# Revit family: Haworth_Compose_Panel_Glass
name_source: partatom
category: Furniture Systems
revit_build: Autodesk Revit 2018 (Build: 20170223_1515(x64)
units: mm (PartAtom-declared; Revit-internal decimal feet)

## family parameters
Always vertical = Yes
Cut with Voids When Loaded = No
OmniClass Number = 23.40.70.14.64.21
OmniClass Title = Systems Furniture
Part Type = Normal
Room Calculation Point = No
Round Connector Dimension = Use Diameter
Shared = No
Work Plane-Based = No

## types (60) — shared parameters
Assembly Code = E2020500
Bottom Trim Width = 1 1/2"
Custom Size = No
Description = Haworth Compose Panel Glass
Frame Depth = 2 3/4"
Frame Width = 3/4"
Glass Finish = Haworth _ Glass _ Clear
Manufacturer = Haworth
Max. Height = 74"
Max. Width = 48"
Min. Height = 42"
Min. Width = 18"
Min/Max Height = 42-74 in. @ 8 in. Increments
Min/Max Width = 18-48 in. @ 6 in. Increments
Model = VZGF
Panel Depth = 1/2"
Raceway Finish = Haworth _ Paint _ Putty
Revision Number = 4
Size = Verify Final Dim. w/ Haworth
Sustainability Info = http://media.haworth.com
Top Trim = Yes
Top Trim Adjuster = 1/8"
Top Trim Width = 1/8"
Trim Depth = 3"
Trim Finish = Haworth _ Paint _ Putty
Trim Thin Profile = Yes
URL = http://www.haworth.com
URL - Product = http://www.haworth.com
Vertical Trim Width = 1/4"
Warranty = http://www.haworth.com

## per-type parameters (varying)
| type | Actual Height | Actual Width | Height | Panel Height | Panel Width | Raceway | Raceway Height | Width |
| 42h 18w No Base Raceway | 41 7/8" | 18" | 42" | 33 3/4" | 16 1/2" | No | 6" | 18" |
| 42h 24w No Base Raceway | 41 7/8" | 24" | 42" | 33 3/4" | 22 1/2" | No | 6" | 24" |
| 42h 30w No Base Raceway | 41 7/8" | 30" | 42" | 33 3/4" | 28 1/2" | No | 6" | 30" |
| 42h 36w No Base Raceway | 41 7/8" | 36" | 42" | 33 3/4" | 34 1/2" | No | 6" | 36" |
| 42h 42w No Base Raceway | 41 7/8" | 42" | 42" | 33 3/4" | 40 1/2" | No | 6" | 42" |
| 42h 48w No Base Raceway | 41 7/8" | 48" | 42" | 33 3/4" | 46 1/2" | No | 6" | 48" |
| 50h 18w No Base Raceway | 49 7/8" | 18" | 50" | 41 3/4" | 16 1/2" | No | 6" | 18" |
| 50h 24w No Base Raceway | 49 7/8" | 24" | 50" | 41 3/4" | 22 1/2" | No | 6" | 24" |
| 50h 30w No Base Raceway | 49 7/8" | 30" | 50" | 41 3/4" | 28 1/2" | No | 6" | 30" |
| 50h 36w No Base Raceway | 49 7/8" | 36" | 50" | 41 3/4" | 34 1/2" | No | 6" | 36" |
| 50h 42w No Base Raceway | 49 7/8" | 42" | 50" | 41 3/4" | 40 1/2" | No | 6" | 42" |
| 50h 48w No Base Raceway | 49 7/8" | 48" | 50" | 41 3/4" | 46 1/2" | No | 6" | 48" |
| 58h 18w No Base Raceway | 57 7/8" | 18" | 58" | 49 3/4" | 16 1/2" | No | 6" | 18" |
| 58h 24w No Base Raceway | 57 7/8" | 24" | 58" | 49 3/4" | 22 1/2" | No | 6" | 24" |
| 58h 30w No Base Raceway | 57 7/8" | 30" | 58" | 49 3/4" | 28 1/2" | No | 6" | 30" |
| 58h 36w No Base Raceway | 57 7/8" | 36" | 58" | 49 3/4" | 34 1/2" | No | 6" | 36" |
| 58h 42w No Base Raceway | 57 7/8" | 42" | 58" | 49 3/4" | 40 1/2" | No | 6" | 42" |
| 58h 48w No Base Raceway | 57 7/8" | 48" | 58" | 49 3/4" | 46 1/2" | No | 6" | 48" |
| 66h 18w No Base Raceway | 65 7/8" | 18" | 66" | 57 3/4" | 16 1/2" | No | 6" | 18" |
| 66h 24w No Base Raceway | 65 7/8" | 24" | 66" | 57 3/4" | 22 1/2" | No | 6" | 24" |
| 66h 30w No Base Raceway | 65 7/8" | 30" | 66" | 57 3/4" | 28 1/2" | No | 6" | 30" |
| 66h 36w No Base Raceway | 65 7/8" | 36" | 66" | 57 3/4" | 34 1/2" | No | 6" | 36" |
| 66h 42w No Base Raceway | 65 7/8" | 42" | 66" | 57 3/4" | 40 1/2" | No | 6" | 42" |
| 66h 48w No Base Raceway | 65 7/8" | 48" | 66" | 57 3/4" | 46 1/2" | No | 6" | 48" |
| 74h 18w No Base Raceway | 73 7/8" | 18" | 74" | 65 3/4" | 16 1/2" | No | 6" | 18" |
| 74h 24w No Base Raceway | 73 7/8" | 24" | 74" | 65 3/4" | 22 1/2" | No | 6" | 24" |
| 74h 30w No Base Raceway | 73 7/8" | 30" | 74" | 65 3/4" | 28 1/2" | No | 6" | 30" |
| 74h 36w No Base Raceway | 73 7/8" | 36" | 74" | 65 3/4" | 34 1/2" | No | 6" | 36" |
| 74h 42w No Base Raceway | 73 7/8" | 42" | 74" | 65 3/4" | 40 1/2" | No | 6" | 42" |
| 74h 48w No Base Raceway | 73 7/8" | 48" | 74" | 65 3/4" | 46 1/2" | No | 6" | 48" |
| 42h 18w With Base Raceway | 41 7/8" | 18" | 42" | 30 1/4" | 16 1/2" | Yes | 9 1/2" | 18" |
| 42h 24w With Base Raceway | 41 7/8" | 24" | 42" | 30 1/4" | 22 1/2" | Yes | 9 1/2" | 24" |
| 42h 30w With Base Raceway | 41 7/8" | 30" | 42" | 30 1/4" | 28 1/2" | Yes | 9 1/2" | 30" |
| 42h 36w With Base Raceway | 41 7/8" | 36" | 42" | 30 1/4" | 34 1/2" | Yes | 9 1/2" | 36" |
| 42h 42w With Base Raceway | 41 7/8" | 42" | 42" | 30 1/4" | 40 1/2" | Yes | 9 1/2" | 42" |
| 42h 48w With Base Raceway | 41 7/8" | 48" | 42" | 30 1/4" | 46 1/2" | Yes | 9 1/2" | 48" |
| 50h 18w With Base Raceway | 49 7/8" | 18" | 50" | 38 1/4" | 16 1/2" | Yes | 9 1/2" | 18" |
| 50h 24w With Base Raceway | 49 7/8" | 24" | 50" | 38 1/4" | 22 1/2" | Yes | 9 1/2" | 24" |
| 50h 30w With Base Raceway | 49 7/8" | 30" | 50" | 38 1/4" | 28 1/2" | Yes | 9 1/2" | 30" |
| 50h 36w With Base Raceway | 49 7/8" | 36" | 50" | 38 1/4" | 34 1/2" | Yes | 9 1/2" | 36" |
| 50h 42w With Base Raceway | 49 7/8" | 42" | 50" | 38 1/4" | 40 1/2" | Yes | 9 1/2" | 42" |
| 50h 48w With Base Raceway | 49 7/8" | 48" | 50" | 38 1/4" | 46 1/2" | Yes | 9 1/2" | 48" |
| 58h 18w With Base Raceway | 57 7/8" | 18" | 58" | 46 1/4" | 16 1/2" | Yes | 9 1/2" | 18" |
| 58h 24w With Base Raceway | 57 7/8" | 24" | 58" | 46 1/4" | 22 1/2" | Yes | 9 1/2" | 24" |
| 58h 30w With Base Raceway | 57 7/8" | 30" | 58" | 46 1/4" | 28 1/2" | Yes | 9 1/2" | 30" |
| 58h 36w With Base Raceway | 57 7/8" | 36" | 58" | 46 1/4" | 34 1/2" | Yes | 9 1/2" | 36" |
| 58h 42w With Base Raceway | 57 7/8" | 42" | 58" | 46 1/4" | 40 1/2" | Yes | 9 1/2" | 42" |
| 58h 48w With Base Raceway | 57 7/8" | 48" | 58" | 46 1/4" | 46 1/2" | Yes | 9 1/2" | 48" |
| 66h 18w With Base Raceway | 65 7/8" | 18" | 66" | 54 1/4" | 16 1/2" | Yes | 9 1/2" | 18" |
| 66h 24w With Base Raceway | 65 7/8" | 24" | 66" | 54 1/4" | 22 1/2" | Yes | 9 1/2" | 24" |
| 66h 30w With Base Raceway | 65 7/8" | 30" | 66" | 54 1/4" | 28 1/2" | Yes | 9 1/2" | 30" |
| 66h 36w With Base Raceway | 65 7/8" | 36" | 66" | 54 1/4" | 34 1/2" | Yes | 9 1/2" | 36" |
| 66h 42w With Base Raceway | 65 7/8" | 42" | 66" | 54 1/4" | 40 1/2" | Yes | 9 1/2" | 42" |
| 66h 48w With Base Raceway | 65 7/8" | 48" | 66" | 54 1/4" | 46 1/2" | Yes | 9 1/2" | 48" |
| 74h 18w With Base Raceway | 73 7/8" | 18" | 74" | 62 1/4" | 16 1/2" | Yes | 9 1/2" | 18" |
| 74h 24w With Base Raceway | 73 7/8" | 24" | 74" | 62 1/4" | 22 1/2" | Yes | 9 1/2" | 24" |
| 74h 30w With Base Raceway | 73 7/8" | 30" | 74" | 62 1/4" | 28 1/2" | Yes | 9 1/2" | 30" |
| 74h 36w With Base Raceway | 73 7/8" | 36" | 74" | 62 1/4" | 34 1/2" | Yes | 9 1/2" | 36" |
| 74h 42w With Base Raceway | 73 7/8" | 42" | 74" | 62 1/4" | 40 1/2" | Yes | 9 1/2" | 42" |
| 74h 48w With Base Raceway | 73 7/8" | 48" | 74" | 62 1/4" | 46 1/2" | Yes | 9 1/2" | 48" |

## geometry (parser evidence)
native form markers: Sweep x10
no freeform markers — native parametric forms only
